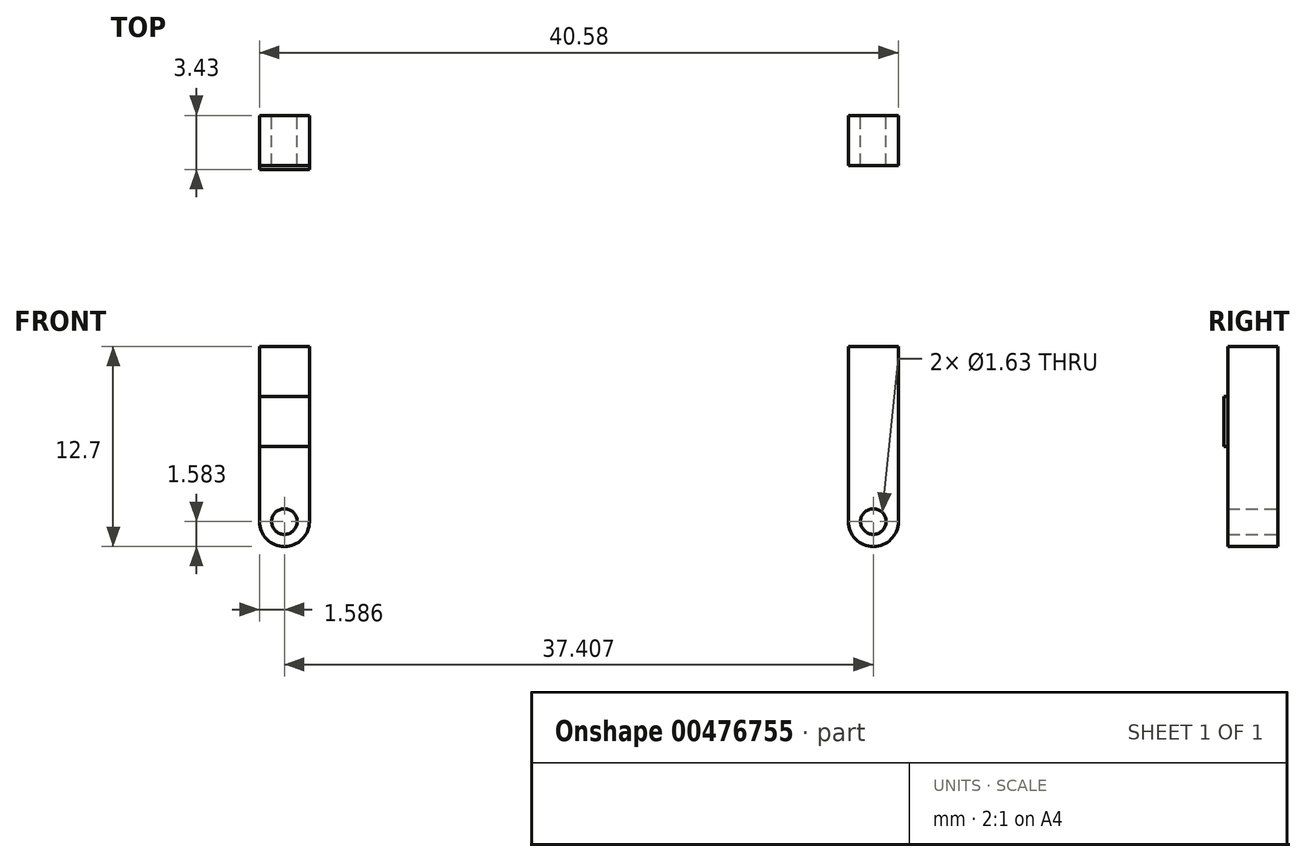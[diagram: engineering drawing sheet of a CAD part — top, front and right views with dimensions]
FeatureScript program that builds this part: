
annotation { "Feature Type Name" : "Feature", "Feature Type Description" : "" }
export const myFeature = defineFeature(function(context is Context, id is Id, definition is map)
    precondition{}
    {
        {
            var Q0;
            Q0=qCreatedBy(makeId("Front.planeOp"),FACE);
            var sketch = newSketch(context, id + "F0", { "sketchPlane" : qUnion([Q0])});
            skLineSegment(sketch, "E0.bottom", {"start": v(-20.3, 6.73) * mm, "end": v(-17.12, 6.73) * mm});
            skLineSegment(sketch, "E0.top", {"start": v(-20.3, -5.97) * mm, "end": v(-17.12, -5.97) * mm});
            skLineSegment(sketch, "E0.left", {"start": v(-20.3, 6.73) * mm, "end": v(-20.3, -5.97) * mm});
            skLineSegment(sketch, "E0.right", {"start": v(-17.12, 6.73) * mm, "end": v(-17.12, -5.97) * mm});
            skPoint(sketch, "E1.centerSnap0", {"position": v(-18.7, -5.97) * mm});
            skCircle(sketch, "E2", {"center": v(-18.7, -4.39) * mm, "radius": 0.81 * mm});
            skSolve(sketch);
        }
        {
            var Q0;
            Q0=makeQuery(id+"F0.imprint","IMPRINT",FACE,{"disambiguationData":[TD([[makeQuery(id+"F0.imprint","IMPRINT",EDGE,{"derivedFrom":sQuery(id+"F0.wireOp",EDGE,"E0.bottom")}),-1.0]])]});
            extrude(context, id + "F1", {"entities" : qUnion([Q0]), "depth" : 3.17 * mm, "symmetric" : true});
        }
        {
            var Q0;
            Q0=makeQuery(id+"F1.opExtrude","SWEPT_EDGE",EDGE,{"disambiguationData":[OSD([sQuery(id+"F0.wireOp",EDGE,"E0.top"),sQuery(id+"F0.wireOp",EDGE,"E0.left")])]});
            var Q1;
            Q1=makeQuery(id+"F1.opExtrude","SWEPT_EDGE",EDGE,{"disambiguationData":[OSD([sQuery(id+"F0.wireOp",EDGE,"E0.top"),sQuery(id+"F0.wireOp",EDGE,"E0.right")])]});
            fillet(context, id + "F2", {"entities" : qUnion([Q0, Q1]), "radius" : 1.59 * mm, "tangentPropagation" : true, "allowEdgeOverflow" : false});
        }
        {
            var Q0;
            Q0=makeQuery(id+"F1.opExtrude","SWEPT_BODY",BODY,{"disambiguationData":[OSD([sQuery(id+"F0.wireOp",EDGE,"E0.bottom"),sQuery(id+"F0.wireOp",EDGE,"E0.top"),sQuery(id+"F0.wireOp",EDGE,"E0.left"),sQuery(id+"F0.wireOp",EDGE,"E0.right"),sQuery(id+"F0.wireOp",EDGE,"E2")])]});
            var Q1;
            Q1=qCreatedBy(makeId("Right.planeOp"),FACE);
            mirror(context, id + "F3", {"entities" : qUnion([Q0]), "mirrorPlane" : qUnion([Q1])});
        }
        {
            var Q0;
            Q0=makeQuery(id+"F1.opExtrude","CAP_FACE",FACE,{"disambiguationData":[OSD([sQuery(id+"F0.wireOp",EDGE,"E0.bottom"),sQuery(id+"F0.wireOp",EDGE,"E0.top"),sQuery(id+"F0.wireOp",EDGE,"E0.left"),sQuery(id+"F0.wireOp",EDGE,"E0.right"),sQuery(id+"F0.wireOp",EDGE,"E2")])],"isStart":false});
            var sketch = newSketch(context, id + "F4", { "sketchPlane" : qUnion([Q0])});
            skLineSegment(sketch, "E3.bottom", {"start": v(-17.12, 0.38) * mm, "end": v(-20.3, 0.38) * mm});
            skLineSegment(sketch, "E3.top", {"start": v(-17.12, 3.55) * mm, "end": v(-20.3, 3.55) * mm});
            skLineSegment(sketch, "E3.left", {"start": v(-17.12, 0.38) * mm, "end": v(-17.12, 3.55) * mm});
            skLineSegment(sketch, "E3.right", {"start": v(-20.3, 0.38) * mm, "end": v(-20.3, 3.55) * mm});
            skPoint(sketch, "E3.middle", {"position": v(-18.7, 1.96) * mm});
            skSolve(sketch);
        }
        {
            var Q0;
            Q0 = qSketchRegion(id + "F4", true);
            extrude(context, id + "F5", {"entities" : qUnion([Q0]), "operationType" : NewBodyOperationType.ADD, "depth" : 0.25 * mm});
        }
    });
